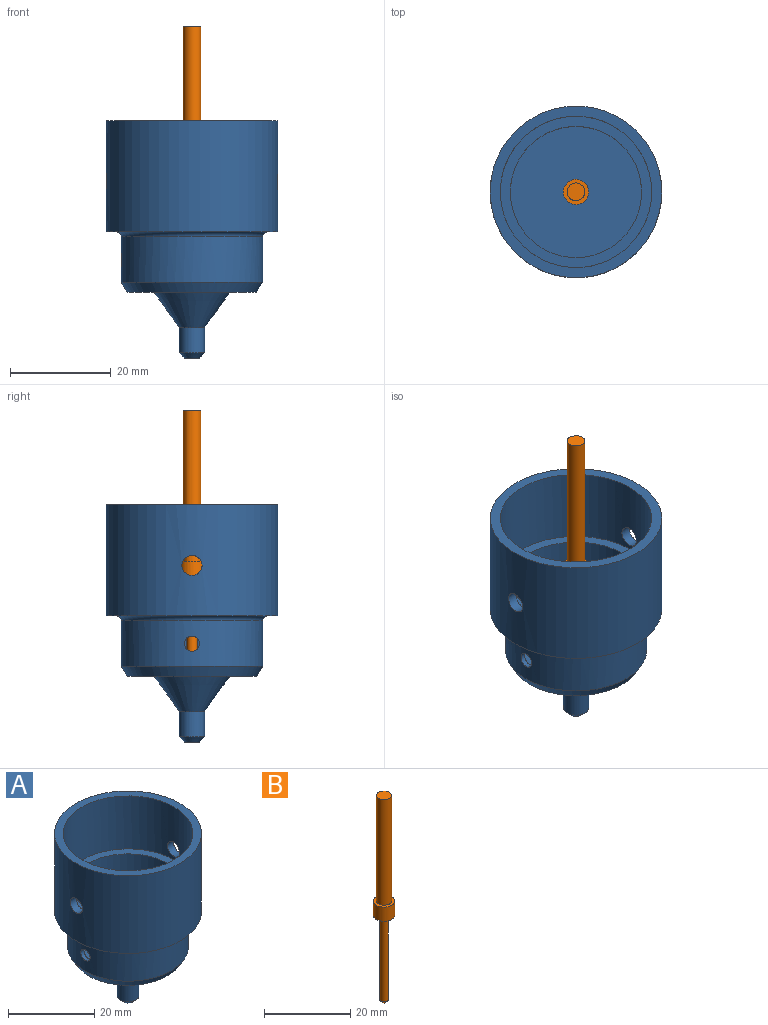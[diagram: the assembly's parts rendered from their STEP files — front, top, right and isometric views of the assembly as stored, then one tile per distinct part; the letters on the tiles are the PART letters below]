
ASSEMBLY  parts=2 mates=1
PART A: 19 faces, bbox 34x34x47 mm
  f0: cylinder r=17mm len=34mm, axis (0,0,-1), area 2324.7mm2, adj f2,f6,f10,f11
  f1: cylinder r=1mm len=18mm, axis (0,0,-1), area 113.1mm2, adj f3,f16
  f2: plane 34x34mm, normal (0,0,1), area 201.1mm2, adj f0,f9
  f3: plane 26x26mm, normal (0,0,1), area 527.8mm2, adj f1,f4
  f4: cylinder r=13mm len=26mm, axis (0,0,1), area 1136.5mm2, adj f3,f8,f12
  f5: cylinder r=14mm len=28mm, axis (0,0,-1), area 784.6mm2, adj f7,f12,f13
  f6: plane 34x34mm, normal (0,0,-1), area 201.1mm2, adj f0,f13
  f7: cone r=8mm half-angle=31deg, axis (0,0,1), area 196.4mm2, adj f5,f14
  f8: plane 30x30mm, normal (0,0,1), area 175.9mm2, adj f4,f9
  f9: cylinder r=15mm len=30mm, axis (0,0,1), area 1388.5mm2, adj f2,f8,f10,f11
  f10: cylinder r=2mm len=4mm, axis (1,0,0), area 25.2mm2, adj f0,f9
  f11: cylinder r=2mm len=4mm, axis (1,0,0), area 25.2mm2, adj f0,f9
  f12: cylinder r=1.5mm len=3mm, axis (1,0,0), area 9.5mm2, adj f4,f5
  f13: torus R=15mm, axis (0,0,-1), area 141.8mm2, adj f5,f6
  f14: plane 25.6x25.6mm, normal (0,0,-1), area 338mm2, adj f7,f17
  f15: cylinder r=2.5mm len=5mm, axis (0,0,1), area 78.5mm2, adj f17,f18
  f16: plane 3x3mm, normal (0,0,-1), area 3.9mm2, adj f1,f18
  f17: cone r=2.5mm half-angle=35.5deg, axis (0,0,1), area 270.3mm2, adj f14,f15
  f18: cone r=1.5mm half-angle=45deg, axis (0,0,1), area 17.8mm2, adj f15,f16
PART B: 7 faces, bbox 5x5x59 mm
  f0: cylinder r=2.5mm len=5mm, axis (0,0,1), area 62.8mm2, adj f3,f5
  f1: cylinder r=1mm len=24mm, axis (0,0,-1), area 150.8mm2, adj f2,f3
  f2: cone r=1mm half-angle=45deg, axis (0,0,1), area 4.4mm2, adj f1
  f3: plane 5x5mm, normal (0,0,-1), area 16.5mm2, adj f0,f1
  f4: cylinder r=1.75mm len=30mm, axis (0,0,1), area 329.9mm2, adj f5,f6
  f5: plane 5x5mm, normal (0,0,1), area 10mm2, adj f0,f4
  f6: plane 3.5x3.5mm, normal (0,0,1), area 9.6mm2, adj f4
PLACE A t=(-101.9,38.62,-130.32)mm fixed
PLACE B rot(axis=(0,0,-1),112.6deg) t=(-101.9,38.62,119.47)mm
MATE cylindrical B.f1 <-> A.f4  axis (0,0,-1) through (-101.9,38.62,144.47)mm
